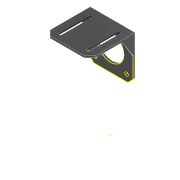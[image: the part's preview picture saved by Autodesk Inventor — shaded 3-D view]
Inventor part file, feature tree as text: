
AUTODESK INVENTOR PART (.ipt)
format: ipt  version: 2022 (Build 260153000, 153)  size: 196,096 bytes
history: native  units: mm
features: sketch x6, extrude x5, chamfer x2, projected_geometry x2
ambient origin geometry x8: Origin, YZ Plane, XZ Plane, XY Plane, X Axis, Y Axis, Z Axis, Center Point
bodies: Solid1 (feature_tree)
feature tree (15):
  extrude  "Extrusion1"  Depth=10.0mm
  extrude  "Extrusion2"  Depth=10.0mm
  chamfer  "Chamfer1"  Distance=3.0mm
  chamfer  "Chamfer2"  Distance=3.0mm
  extrude  "Extrusion3"  Depth=65.0mm TaperAngle=0.0deg
  extrude  "Extrusion4"  Depth=2.5mm TaperAngle=45.0deg
  extrude  "Extrusion5"  Depth=2.5mm TaperAngle=45.0deg
  sketch  "Sketch7"  dims[d7=8.0mm d8=3.0mm d9=0.0mm d10=3.0mm d11=65.0mm d12=0.0mm d13=8.0mm d14=2.0mm d15=45.0deg d16=8.0mm d17=2.0mm d18=45.0deg d19=25.0mm d20=16.0mm d21=3.0mm d22=0.0mm d23=3.0mm d24=0.0mm d25=10.0mm d26=5.0mm d27=50.0mm d28=10.0mm d29=5.0mm d30=2.5mm d31=0.0mm d32=0.0mm]
  sketch  "Sketch1"  dims[d0=10.0mm d1=10.0mm]
  sketch  "Sketch2"  dims[d2=10.0mm d3=10.0mm]
  sketch  "Sketch3"  dims[d4=8.0mm]
  sketch  "Sketch4"  dims[d5=8.0mm]
  projected_geometry  "Projected Loop1"
  sketch  "Sketch5"  dims[d6=8.0mm]
  projected_geometry  "Projected Loop2"
